# Revit family: Hager-IC-Flush_mounted-IP30-With_Cover-With_DIN-Hosted-ES-es
name_source: partatom
category: Electrical Equipment
units: mm (PartAtom-declared; Revit-internal decimal feet)

## family parameters
Cut with Voids When Loaded = No
Host = Face
Maintain Annotation Orientation = Yes
Panel Configuration = Two Columns, Circuits Across
Part Type = Panelboard
Room Calculation Point = No
Round Connector Dimension = Use Diameter
Shared = No

## types (12) — shared parameters
BC_MODEL_ID = 1554343
BC_OBJECT_ID = 513882
BC_OBJECT_VERSION = #3
Code hager = ADD-EC000214_EU
EF000003 - Método de montaje = Montado empotrado (escayola)
EF000007 - Color = Blanco
EF000024 - Resistente a UV = No
EF000116 - Número RAL = 9010
EF000118 - Con placa de montaje = No
EF000218 - Profundidad de instalación = 72 mm  [stored 0.23622 ft]
EF001062 - Versión de CEM = No
EF001088 - Posibilidad de extensión = Yes
EF001134 - Carril DIN = Yes
EF004462 - Tipo de cierre = Otros
EF005474 - Grado de protección (IP) = IP30
EF006244 - Tapa/puerta transparente = No
EF006306 - Con candado = No
EF009212 - Versión de la cubierta = Cerrado
EF015776 - Borne de tierra = No
EF015777 - Borne neutro = No
EF015941 - Puerta de transmisión de señal = Yes
ETIM class code = EC000214
ETIM class name = Small distribution board
HG000001 - Número de columnas = 1
HG000002-with door or cover-es = Yes
HG000003-Range-es = IC
HG000005-Thickness-es = 2 mm  [stored 0.00656168 ft]
HG000006-Flush mounted-es = Yes
HG000009-Double swing door-es = No
HG000010-Asymmetric doors-es = No
HG000011-Empty rows from bottom-es = No
HG000012-Door swing angle-es = 90.00°
HG000013-Door on the left-es = No
HG000014-Door on the right-es = Yes
HG000015-Clearance visibility-es = Yes
HG000016-Door 3D visibility-es = Yes
HG000017-Distance between poles-es = 18 mm  [stored 0.0590551 ft]
HG000060-RAL-number = 9010
HG000099-Onfly Template ID-es-ES = 507532
Manufacturer = Hager
Name = IC-Flush_mounted-IP30-With_Cover-With_DIN-ES
Name BIM&CO = Electricity
Name hager = ADD_Enclosures_EC000214
Uniformat = Low Tension Service & Dist.
Uniformat code = D501001
zero-valued in all types: Default Elevation, EF001131 - Profundidad interna, HG000007-Number of empty columns-es, HG000008-Number of empty rows-es

## per-type parameters (varying)
| type | BC_VARIANT_ID | EF000008 - Anchura | EF000040 - Altura | EF000049 - Profundidad | EF000266 - Número de filas | EF000332 - Altura de la instalación | EF000846 - Anchura de montaje | EF002950 - Ancho en número de espacios modulares | HG000004-Manufacturer reference-es | HGEF000266-Número de filas | HGEF0002950-Ancho en número de espacios modulares |
| IC-Flush_mounted_W236_H206_D91_8_Modular_Spacing-VR108NE | 1178963 | 236 mm | 206 mm  [stored 0.675853 ft] | 91 mm  [stored 0.298556 ft] | 1 | 188 mm  [stored 0.616798 ft] | 218 mm  [stored 0.715223 ft] | 8 | VR108NE | 1 | 8 |
| IC-Flush_mounted_W236_H206_D91_8_Modular_Spacing-VR108NH | 1178964 | 236 mm | 206 mm  [stored 0.675853 ft] | 91 mm  [stored 0.298556 ft] | 1 | 188 mm  [stored 0.616798 ft] | 218 mm  [stored 0.715223 ft] | 8 | VR108NH | 1 | 8 |
| IC-Flush_mounted_W308_H226_D91_12_Modular_Spacing-VR112NE | 1178965 | 308 mm  [stored 1.0105 ft] | 226 mm  [stored 0.74147 ft] | 91 mm  [stored 0.298556 ft] | 1 | 208 mm | 290 mm  [stored 0.951444 ft] | 12 | VR112NE | 1 | 12 |
| IC-Flush_mounted_W308_H226_D91_12_Modular_Spacing-VR112NH | 1178966 | 308 mm  [stored 1.0105 ft] | 226 mm  [stored 0.74147 ft] | 91 mm  [stored 0.298556 ft] | 1 | 208 mm | 290 mm  [stored 0.951444 ft] | 12 | VR112NH | 1 | 12 |
| IC-Flush_mounted_W416_H226_D91_18_Modular_Spacing-VR118NE | 1178967 | 416 mm | 226 mm  [stored 0.74147 ft] | 91 mm  [stored 0.298556 ft] | 1 | 208 mm | 398 mm  [stored 1.30577 ft] | 18 | VR118NE | 1 | 18 |
| IC-Flush_mounted_W416_H226_D91_18_Modular_Spacing-VR118NH | 1178968 | 416 mm | 226 mm  [stored 0.74147 ft] | 91 mm  [stored 0.298556 ft] | 1 | 208 mm | 398 mm  [stored 1.30577 ft] | 18 | VR118NH | 1 | 18 |
| IC-Flush_mounted_W308_H351_D93_12_Modular_Spacing-VR212NE | 1178969 | 308 mm  [stored 1.0105 ft] | 351 mm  [stored 1.15157 ft] | 93 mm  [stored 0.305118 ft] | 2 | 333 mm  [stored 1.09252 ft] | 290 mm  [stored 0.951444 ft] | 12 | VR212NE | 2 | 12 |
| IC-Flush_mounted_W308_H351_D93_12_Modular_Spacing-VR212NE1 | 1178970 | 308 mm  [stored 1.0105 ft] | 351 mm  [stored 1.15157 ft] | 93 mm  [stored 0.305118 ft] | 2 | 333 mm  [stored 1.09252 ft] | 290 mm  [stored 0.951444 ft] | 12 | VR212NE1 | 2 | 12 |
| IC-Flush_mounted_W308_H351_D93_12_Modular_Spacing-VR212NE2 | 1178971 | 308 mm  [stored 1.0105 ft] | 351 mm  [stored 1.15157 ft] | 93 mm  [stored 0.305118 ft] | 2 | 333 mm  [stored 1.09252 ft] | 290 mm  [stored 0.951444 ft] | 12 | VR212NE2 | 2 | 12 |
| IC-Flush_mounted_W308_H351_D93_12_Modular_Spacing-VR212NE3 | 1178972 | 308 mm  [stored 1.0105 ft] | 351 mm  [stored 1.15157 ft] | 93 mm  [stored 0.305118 ft] | 2 | 333 mm  [stored 1.09252 ft] | 290 mm  [stored 0.951444 ft] | 12 | VR212NE3 | 2 | 12 |
| IC-Flush_mounted_W308_H351_D93_12_Modular_Spacing-VR212NH | 1178973 | 308 mm  [stored 1.0105 ft] | 351 mm  [stored 1.15157 ft] | 93 mm  [stored 0.305118 ft] | 2 | 333 mm  [stored 1.09252 ft] | 290 mm  [stored 0.951444 ft] | 12 | VR212NH | 2 | 12 |
| IC-Flush_mounted_W308_H351_D93_12_Modular_Spacing-VR212NH1 | 1178974 | 308 mm  [stored 1.0105 ft] | 351 mm  [stored 1.15157 ft] | 93 mm  [stored 0.305118 ft] | 2 | 333 mm  [stored 1.09252 ft] | 290 mm  [stored 0.951444 ft] | 12 | VR212NH1 | 2 | 12 |

note: column(s) folded — value = type name in every type: Reference

note: [stored X ft] marks values corroborated as IEEE doubles in the binary element streams (Revit-internal decimal feet)

## geometry (parser evidence)
native form markers: Sweep x13
no freeform markers — native parametric forms only
